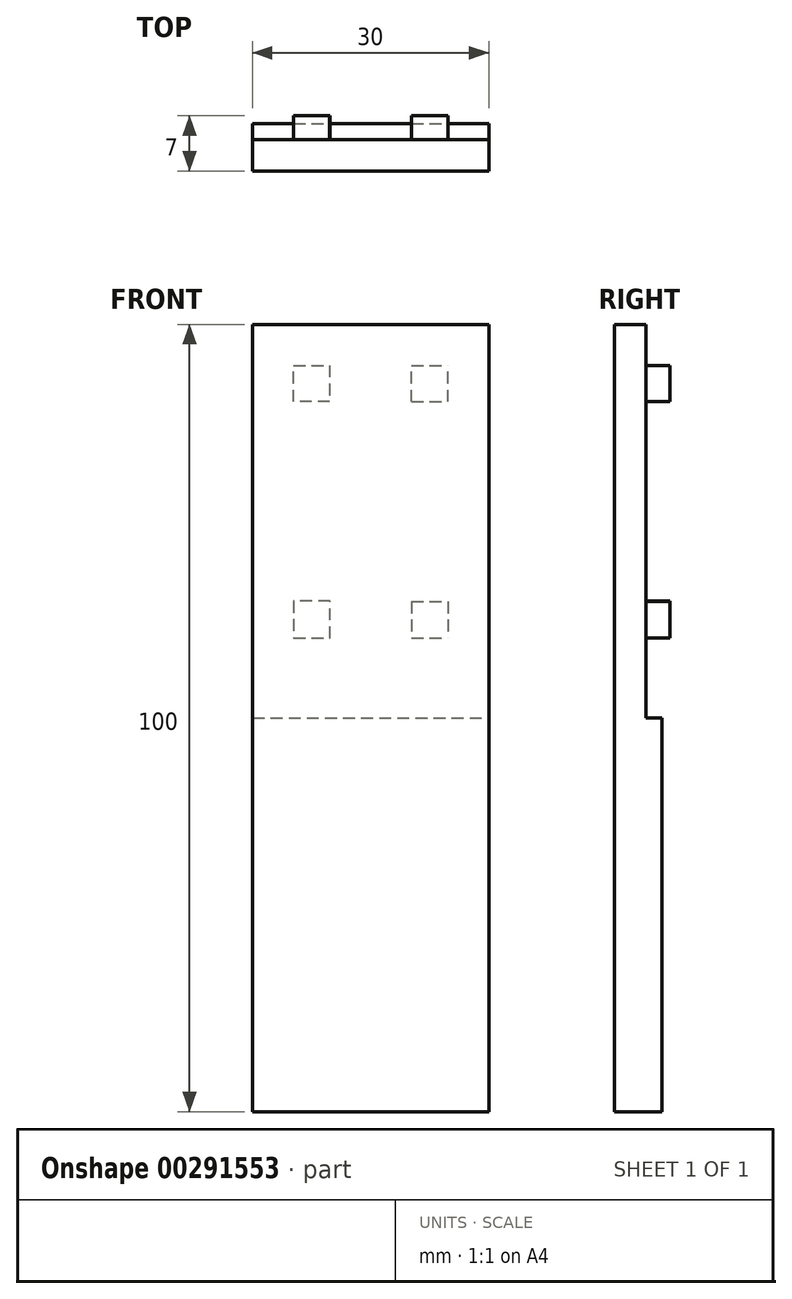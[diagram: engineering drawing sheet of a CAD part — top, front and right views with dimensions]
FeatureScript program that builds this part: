
annotation { "Feature Type Name" : "Feature", "Feature Type Description" : "" }
export const myFeature = defineFeature(function(context is Context, id is Id, definition is map)
    precondition{}
    {
        {
            var Q0;
            Q0=qCreatedBy(makeId("Top.planeOp"),FACE);
            var sketch = newSketch(context, id + "F0", { "sketchPlane" : qUnion([Q0])});
            skLineSegment(sketch, "E0.bottom", {"start": v(-15, 3) * mm, "end": v(15, 3) * mm});
            skLineSegment(sketch, "E0.top", {"start": v(-15, -3) * mm, "end": v(15, -3) * mm});
            skLineSegment(sketch, "E0.left", {"start": v(-15, 3) * mm, "end": v(-15, -3) * mm});
            skLineSegment(sketch, "E0.right", {"start": v(15, 3) * mm, "end": v(15, -3) * mm});
            skSolve(sketch);
        }
        {
            var Q0;
            Q0=qSketchRegion(id+"F0",true);
            extrude(context, id + "F1", {"entities" : qUnion([Q0]), "depth" : 100 * mm, "offsetDistance" : 25 * mm});
        }
        {
            var Q0;
            Q0=makeQuery(id+"F1.opExtrude","SWEPT_FACE",FACE,{"disambiguationData":[OSD([sQuery(id+"F0.wireOp",EDGE,"E0.right")])]});
            var sketch = newSketch(context, id + "F2", { "sketchPlane" : qUnion([Q0])});
            skLineSegment(sketch, "E1.bottom", {"start": v(1, 100) * mm, "end": v(3, 100) * mm});
            skLineSegment(sketch, "E1.top", {"start": v(1, 50) * mm, "end": v(3, 50) * mm});
            skLineSegment(sketch, "E1.left", {"start": v(1, 100) * mm, "end": v(1, 50) * mm});
            skLineSegment(sketch, "E1.right", {"start": v(3, 100) * mm, "end": v(3, 50) * mm});
            skSolve(sketch);
        }
        {
            var Q0;
            Q0=qSketchRegion(id+"F2",true);
            extrude(context, id + "F3", {"entities" : qUnion([Q0]), "operationType" : NewBodyOperationType.REMOVE, "endBound" : BoundingType.UP_TO_NEXT, "oppositeDirection" : true, "depth" : 25 * mm, "offsetDistance" : 25 * mm});
        }
        {
            var Q0;
            Q0=makeQuery(id+"F3.boolean.opBoolean","COPY",FACE,{"derivedFrom":makeQuery(id+"F3.opExtrude","SWEPT_FACE",FACE,{"disambiguationData":[OSD([sQuery(id+"F2.wireOp",EDGE,"E1.left")])]})});
            var sketch = newSketch(context, id + "F4", { "sketchPlane" : qUnion([Q0])});
            skLineSegment(sketch, "E2.0", {"start": v(-5.2, 94.8) * mm, "end": v(-9.8, 94.8) * mm});
            skLineSegment(sketch, "E2.1", {"start": v(-5.2, 90.2) * mm, "end": v(-5.2, 94.8) * mm});
            skLineSegment(sketch, "E2.2", {"start": v(-5.2, 90.2) * mm, "end": v(-9.8, 90.2) * mm});
            skLineSegment(sketch, "E2.3", {"start": v(-9.8, 90.2) * mm, "end": v(-9.8, 94.8) * mm});
            skLineSegment(sketch, "E3.0", {"start": v(9.8, 94.8) * mm, "end": v(5.2, 94.8) * mm});
            skLineSegment(sketch, "E3.1", {"start": v(9.8, 90.2) * mm, "end": v(9.8, 94.8) * mm});
            skLineSegment(sketch, "E3.2", {"start": v(5.2, 90.2) * mm, "end": v(9.8, 90.2) * mm});
            skLineSegment(sketch, "E3.3", {"start": v(5.2, 94.8) * mm, "end": v(5.2, 90.2) * mm});
            skLineSegment(sketch, "E4.0", {"start": v(-5.2, 64.8) * mm, "end": v(-9.8, 64.8) * mm});
            skLineSegment(sketch, "E4.1", {"start": v(-5.2, 64.8) * mm, "end": v(-5.2, 60.2) * mm});
            skLineSegment(sketch, "E4.2", {"start": v(-5.2, 60.2) * mm, "end": v(-9.8, 60.2) * mm});
            skLineSegment(sketch, "E4.3", {"start": v(-9.8, 64.8) * mm, "end": v(-9.8, 60.2) * mm});
            skLineSegment(sketch, "E5.0", {"start": v(5.14, 64.86) * mm, "end": v(9.8, 64.86) * mm});
            skLineSegment(sketch, "E5.1", {"start": v(5.14, 60.14) * mm, "end": v(5.14, 64.86) * mm});
            skLineSegment(sketch, "E5.2", {"start": v(9.8, 60.14) * mm, "end": v(5.14, 60.14) * mm});
            skLineSegment(sketch, "E5.3", {"start": v(9.8, 64.86) * mm, "end": v(9.8, 60.14) * mm});
            skSolve(sketch);
        }
        {
            var Q0;
            Q0=qSketchRegion(id+"F4",true);
            extrude(context, id + "F5", {"entities" : qUnion([Q0]), "operationType" : NewBodyOperationType.ADD, "depth" : 3 * mm, "offsetDistance" : 25 * mm});
        }
    });
